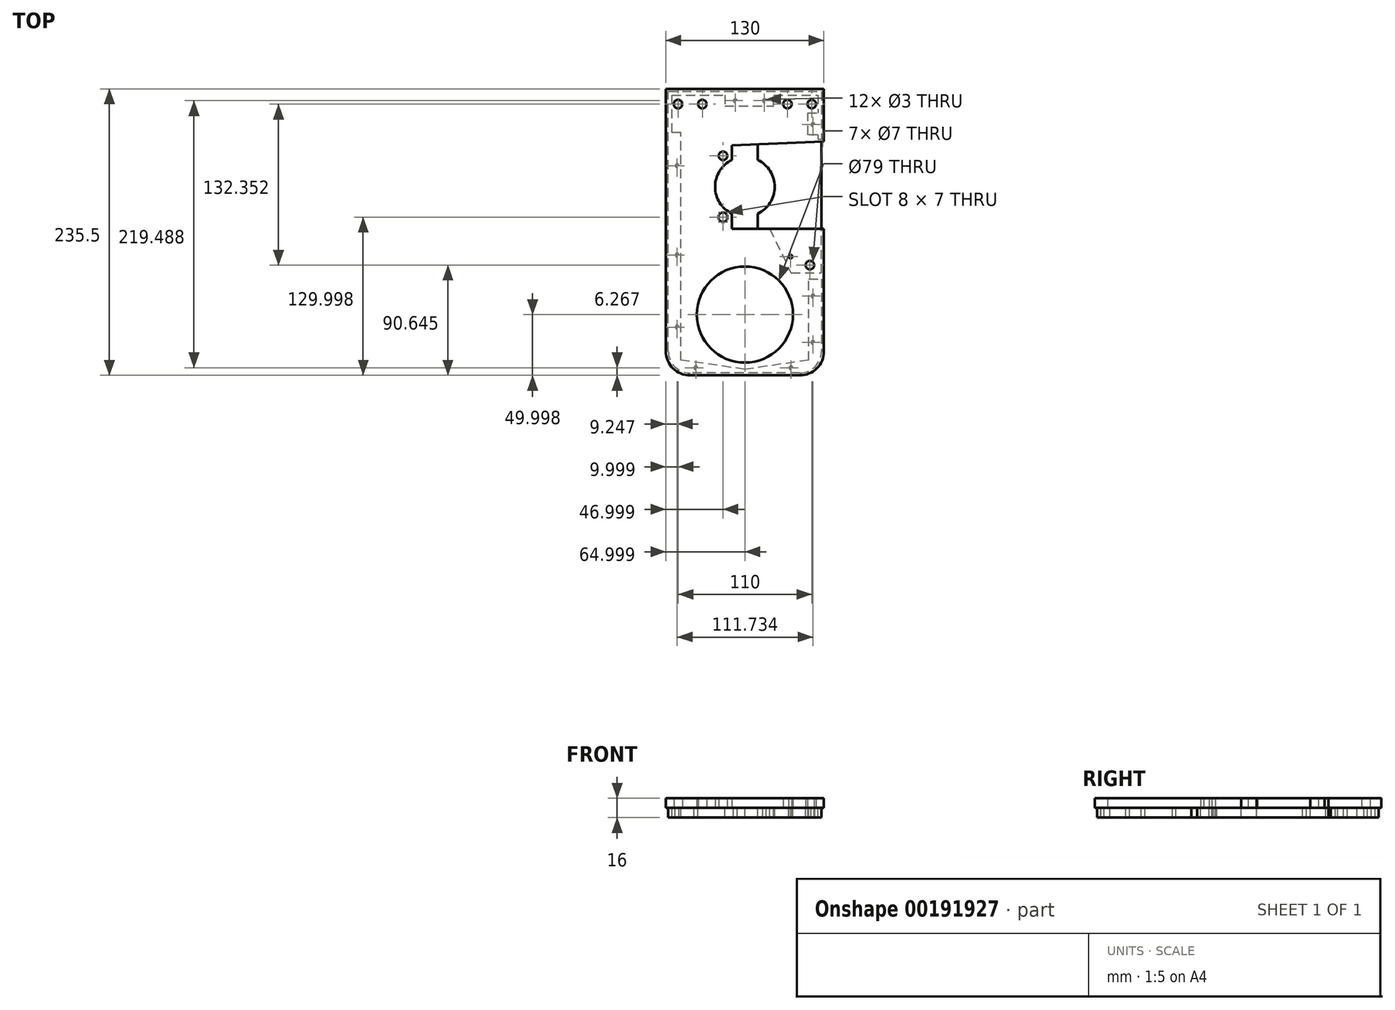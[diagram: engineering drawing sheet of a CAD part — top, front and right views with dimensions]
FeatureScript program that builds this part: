
annotation { "Feature Type Name" : "Feature", "Feature Type Description" : "" }
export const myFeature = defineFeature(function(context is Context, id is Id, definition is map)
    precondition{}
    {
        {
            var Q0;
            Q0=qCreatedBy(makeId("Top.planeOp"),FACE);
            var sketch = newSketch(context, id + "F0", { "sketchPlane" : qUnion([Q0])});
            skCircle(sketch, "E0", {"center": v(-75.48, 27.05) * mm, "radius": 3.5 * mm});
            skCircle(sketch, "E1", {"center": v(-55.48, 27.05) * mm, "radius": 3.5 * mm});
            skCircle(sketch, "E2", {"center": v(14.52, 27.05) * mm, "radius": 3.5 * mm});
            skCircle(sketch, "E3", {"center": v(34.52, 27.05) * mm, "radius": 3.5 * mm});
            skLineSegment(sketch, "E4", {"start": v(-85.48, 39.55) * mm, "end": v(44.52, 39.55) * mm});
            skLineSegment(sketch, "E5", {"start": v(44.52, 39.55) * mm, "end": v(44.52, 14.55) * mm});
            skLineSegment(sketch, "E6", {"start": v(44.52, 14.55) * mm, "end": v(-31.06, 14.55) * mm});
            skLineSegment(sketch, "E7", {"start": v(-31.06, 14.55) * mm, "end": v(-31.06, -96.45) * mm});
            skLineSegment(sketch, "E8", {"start": v(-85.48, -95.95) * mm, "end": v(-85.48, 39.55) * mm});
            skLineSegment(sketch, "E9", {"start": v(-85.48, -95.95) * mm, "end": v(-85.48, -195.95) * mm});
            skLineSegment(sketch, "E10", {"start": v(-85.48, -195.95) * mm, "end": v(44.52, -195.95) * mm});
            skLineSegment(sketch, "E11", {"start": v(44.52, -195.95) * mm, "end": v(44.52, -96.45) * mm});
            skLineSegment(sketch, "E12", {"start": v(44.52, -96.45) * mm, "end": v(-31.06, -96.45) * mm});
            skCircle(sketch, "E13", {"center": v(-20.48, -145.95) * mm, "radius": 39.5 * mm});
            skLineSegment(sketch, "E14", {"start": v(-85.48, -95.95) * mm, "end": v(44.52, -195.95) * mm, "construction": true});
            skLineSegment(sketch, "E15", {"start": v(-85.48, -195.95) * mm, "end": v(44.52, -96.45) * mm, "construction": true});
            skLineSegment(sketch, "E16", {"start": v(-20.48, 39.55) * mm, "end": v(-20.48, -195.95) * mm, "construction": true});
            skLineSegment(sketch, "E17", {"start": v(-85.48, -40.95) * mm, "end": v(48.26, -40.95) * mm, "construction": true});
            skCircle(sketch, "E18", {"center": v(-20.48, -40.95) * mm, "radius": 21.5 * mm, "construction": true});
            skLineSegment(sketch, "E19", {"start": v(-38.48, -15.45) * mm, "end": v(-2.48, -15.45) * mm, "construction": true});
            skLineSegment(sketch, "E20", {"start": v(-2.48, -15.45) * mm, "end": v(-2.48, -66.45) * mm, "construction": true});
            skLineSegment(sketch, "E21", {"start": v(-2.48, -66.45) * mm, "end": v(-38.48, -66.45) * mm, "construction": true});
            skLineSegment(sketch, "E22", {"start": v(-38.48, -66.45) * mm, "end": v(-38.48, -15.45) * mm, "construction": true});
            skCircle(sketch, "E23", {"center": v(-38.48, -15.45) * mm, "radius": 3.5 * mm});
            skCircle(sketch, "E24", {"center": v(-38.48, -66.45) * mm, "radius": 3.5 * mm});
            skCircle(sketch, "E25.0", {"center": v(-20.48, -40.95) * mm, "radius": 24.5 * mm});
            skCircle(sketch, "E26", {"center": v(-38.48, -65.45) * mm, "radius": 3.5 * mm});
            skLineSegment(sketch, "E27", {"start": v(-41.98, -66.45) * mm, "end": v(-41.98, -65.45) * mm});
            skLineSegment(sketch, "E28", {"start": v(-34.98, -66.45) * mm, "end": v(-34.98, -65.45) * mm});
            skLineSegment(sketch, "E29", {"start": v(44.52, 14.55) * mm, "end": v(44.52, -19.45) * mm});
            skLineSegment(sketch, "E30", {"start": v(44.52, -19.45) * mm, "end": v(8.15, -19.45) * mm});
            skLineSegment(sketch, "E31", {"start": v(8.15, -19.45) * mm, "end": v(6.73, 14.55) * mm});
            skLineSegment(sketch, "E32", {"start": v(-31.06, -75.45) * mm, "end": v(44.52, -75.45) * mm});
            skLineSegment(sketch, "E33", {"start": v(44.52, -75.45) * mm, "end": v(44.52, -96.45) * mm});
            skLineSegment(sketch, "E34", {"start": v(-31.06, -6.86) * mm, "end": v(7.56, -5.25) * mm});
            skLineSegment(sketch, "E35", {"start": v(7.56, -5.25) * mm, "end": v(44.52, -3.7) * mm});
            skCircle(sketch, "E36", {"center": v(32.95, -105.3) * mm, "radius": 3.5 * mm});
            skSolve(sketch);
        }
        {
            var Q0;
            Q0=makeQuery(id+"F0.imprint","IMPRINT",FACE,{"disambiguationData":[TD([[makeQuery(id+"F0.imprint","IMPRINT",EDGE,{"derivedFrom":sQuery(id+"F0.wireOp",EDGE,"E0")}),-1.0]])]});
            var Q1;
            {var subQ0=sQuery(id+"F0.wireOp",EDGE,"ye42K3yO-AjDR-pxzV-AlUx-Db0uiflmWcsa");Q1=makeQuery(id+"F0.imprint","IMPRINT",FACE,{"disambiguationData":[TD([[makeQuery(id+"F0.imprint","IMPRINT",EDGE,{"derivedFrom":subQ0}),1.0]])]});}
            var Q2;
            {var subQ0=sQuery(id+"F0.wireOp",EDGE,"E12");Q2=makeQuery(id+"F0.imprint","IMPRINT",FACE,{"disambiguationData":[TD([[makeQuery(id+"F0.imprint","IMPRINT",EDGE,{"derivedFrom":subQ0}),-1.0]])]});}
            var Q3;
            {var subQ0=sQuery(id+"F0.wireOp",EDGE,"E6");Q3=makeQuery(id+"F0.imprint","IMPRINT",FACE,{"disambiguationData":[TD([[makeQuery(id+"F0.imprint","IMPRINT",EDGE,{"derivedFrom":subQ0}),1.0]])]});}
            extrude(context, id + "F1", {"entities" : qUnion([Q0, Q1, Q2, Q3]), "depth" : 8 * mm});
        }
        {
            var Q0;
            Q0=makeQuery(id+"F1.opExtrude","SWEPT_EDGE",EDGE,{"disambiguationData":[OSD([sQuery(id+"F0.wireOp",EDGE,"E9"),sQuery(id+"F0.wireOp",EDGE,"E10")])]});
            var Q1;
            Q1=makeQuery(id+"F1.opExtrude","SWEPT_EDGE",EDGE,{"disambiguationData":[OSD([sQuery(id+"F0.wireOp",EDGE,"E11"),sQuery(id+"F0.wireOp",EDGE,"E12")])]});
            var Q2;
            Q2=makeQuery(id+"F1.opExtrude","SWEPT_EDGE",EDGE,{"disambiguationData":[OSD([sQuery(id+"F0.wireOp",EDGE,"E10"),sQuery(id+"F0.wireOp",EDGE,"E11")])]});
            fillet(context, id + "F2", {"entities" : qUnion([Q0, Q1, Q2]), "radius" : 20 * mm, "tangentPropagation" : true, "allowEdgeOverflow" : false});
        }
        {
            var Q0;
            Q0=makeQuery(id+"F1.opExtrude","CAP_FACE",FACE,{"disambiguationData":[OSD([sQuery(id+"F0.wireOp",EDGE,"E0"),sQuery(id+"F0.wireOp",EDGE,"E1"),sQuery(id+"F0.wireOp",EDGE,"E2"),sQuery(id+"F0.wireOp",EDGE,"E3"),sQuery(id+"F0.wireOp",EDGE,"E4"),sQuery(id+"F0.wireOp",EDGE,"E5"),sQuery(id+"F0.wireOp",EDGE,"E7"),sQuery(id+"F0.wireOp",EDGE,"E8"),sQuery(id+"F0.wireOp",EDGE,"E9"),sQuery(id+"F0.wireOp",EDGE,"E10"),sQuery(id+"F0.wireOp",EDGE,"E11"),sQuery(id+"F0.wireOp",EDGE,"E13"),sQuery(id+"F0.wireOp",EDGE,"E23"),sQuery(id+"F0.wireOp",EDGE,"E24"),sQuery(id+"F0.wireOp",EDGE,"E25.0"),sQuery(id+"F0.wireOp",EDGE,"E26"),sQuery(id+"F0.wireOp",EDGE,"E27"),sQuery(id+"F0.wireOp",EDGE,"E28"),sQuery(id+"F0.wireOp",EDGE,"E29"),sQuery(id+"F0.wireOp",EDGE,"E32"),sQuery(id+"F0.wireOp",EDGE,"E33"),sQuery(id+"F0.wireOp",EDGE,"E34"),sQuery(id+"F0.wireOp",EDGE,"E35"),sQuery(id+"F0.wireOp",EDGE,"E36")])],"isStart":true});
            var sketch = newSketch(context, id + "F3", { "sketchPlane" : qUnion([Q0])});
            skLineSegment(sketch, "E37.0", {"start": v(39.52, -34.55) * mm, "end": v(39.52, 1.79) * mm});
            skLineSegment(sketch, "E37.1", {"start": v(-80.48, -34.55) * mm, "end": v(39.52, -34.55) * mm});
            skLineSegment(sketch, "E37.2", {"start": v(-80.48, 175.95) * mm, "end": v(-80.48, -34.55) * mm});
            skLineSegment(sketch, "E37.3", {"start": v(39.52, 175.95) * mm, "end": v(39.52, 77.45) * mm});
            skArc(sketch, "E37.4", {"start": v(39.52, 175.95) * mm, "mid": v(35.13, 186.56) * mm, "end": v(24.52, 190.95) * mm});
            skLineSegment(sketch, "E37.5", {"start": v(-65.48, 190.95) * mm, "end": v(24.52, 190.95) * mm});
            skArc(sketch, "E37.6", {"start": v(-65.48, 190.95) * mm, "mid": v(-76.09, 186.56) * mm, "end": v(-80.48, 175.95) * mm});
            skArc(sketch, "E38.0", {"start": v(42.52, 175.95) * mm, "mid": v(37.25, 188.68) * mm, "end": v(24.52, 193.95) * mm});
            skLineSegment(sketch, "E38.1", {"start": v(42.52, -37.55) * mm, "end": v(42.52, 1.79) * mm});
            skLineSegment(sketch, "E38.2", {"start": v(-83.48, -37.55) * mm, "end": v(42.52, -37.55) * mm});
            skLineSegment(sketch, "E38.3", {"start": v(-83.48, 175.95) * mm, "end": v(-83.48, -37.55) * mm});
            skArc(sketch, "E38.4", {"start": v(-65.48, 193.95) * mm, "mid": v(-78.2, 188.68) * mm, "end": v(-83.48, 175.95) * mm});
            skLineSegment(sketch, "E38.5", {"start": v(42.52, 1.79) * mm, "end": v(-33.06, 4.95) * mm});
            skLineSegment(sketch, "E38.6", {"start": v(24.52, 193.95) * mm, "end": v(-65.48, 193.95) * mm});
            skLineSegment(sketch, "E38.7", {"start": v(-33.06, 4.95) * mm, "end": v(-33.06, 22.3) * mm});
            skArc(sketch, "E38.8", {"start": v(-33.06, 22.3) * mm, "mid": v(-42.98, 40.95) * mm, "end": v(-33.06, 59.6) * mm});
            skLineSegment(sketch, "E38.9", {"start": v(-33.06, 59.6) * mm, "end": v(-33.06, 77.45) * mm});
            skLineSegment(sketch, "E38.10", {"start": v(-33.06, 77.45) * mm, "end": v(42.52, 77.45) * mm});
            skLineSegment(sketch, "E38.11", {"start": v(42.52, 77.45) * mm, "end": v(42.52, 175.95) * mm});
            skLineSegment(sketch, "E39", {"start": v(39.52, 77.45) * mm, "end": v(42.52, 77.45) * mm});
            skLineSegment(sketch, "E40", {"start": v(39.52, 1.79) * mm, "end": v(42.52, 1.79) * mm});
            skLineSegment(sketch, "E41", {"start": v(39.52, 116.59) * mm, "end": v(42.52, 116.59) * mm});
            skLineSegment(sketch, "E42", {"start": v(24.52, 190.95) * mm, "end": v(39.52, 175.95) * mm});
            skLineSegment(sketch, "E43", {"start": v(-65.48, 190.95) * mm, "end": v(-80.48, 175.95) * mm});
            skLineSegment(sketch, "E44", {"start": v(32.02, 183.45) * mm, "end": v(32.02, 116.59) * mm});
            skLineSegment(sketch, "E45", {"start": v(32.02, 116.59) * mm, "end": v(39.52, 116.59) * mm});
            skLineSegment(sketch, "E46", {"start": v(32.02, 183.45) * mm, "end": v(-20.48, 190.95) * mm});
            skLineSegment(sketch, "E47", {"start": v(-72.98, 183.45) * mm, "end": v(-72.98, -3.75) * mm});
            skLineSegment(sketch, "E48", {"start": v(-72.98, -3.75) * mm, "end": v(-83.48, -3.75) * mm});
            skLineSegment(sketch, "E49", {"start": v(-36.99, -34.55) * mm, "end": v(-36.99, -25.55) * mm});
            skLineSegment(sketch, "E50", {"start": v(-36.99, -25.55) * mm, "end": v(3.21, -25.55) * mm});
            skLineSegment(sketch, "E51", {"start": v(3.21, -25.55) * mm, "end": v(3.21, -34.55) * mm});
            skLineSegment(sketch, "E52", {"start": v(-20.48, 190.95) * mm, "end": v(-72.98, 183.45) * mm});
            skLineSegment(sketch, "E53", {"start": v(39.52, -29.73) * mm, "end": v(34.1, -34.55) * mm});
            skLineSegment(sketch, "E54", {"start": v(-80.48, -29.93) * mm, "end": v(-73.16, -34.55) * mm});
            skLineSegment(sketch, "E55", {"start": v(39.52, -1.75) * mm, "end": v(31.23, -1.75) * mm});
            skLineSegment(sketch, "E56", {"start": v(31.23, -1.75) * mm, "end": v(31.23, -19.82) * mm});
            skLineSegment(sketch, "E57", {"start": v(31.23, -19.82) * mm, "end": v(39.52, -19.82) * mm});
            skCircle(sketch, "E58", {"center": v(35.5, 168.95) * mm, "radius": 1.5 * mm});
            skCircle(sketch, "E59", {"center": v(35.5, 130.7) * mm, "radius": 1.5 * mm});
            skCircle(sketch, "E60", {"center": v(-60.8, 189.68) * mm, "radius": 1.5 * mm});
            skCircle(sketch, "E61", {"center": v(-76.23, 156.28) * mm, "radius": 1.5 * mm});
            skCircle(sketch, "E62", {"center": v(-76.23, 97.05) * mm, "radius": 1.5 * mm});
            skCircle(sketch, "E63", {"center": v(-76.23, 23.57) * mm, "radius": 1.5 * mm});
            skCircle(sketch, "E64", {"center": v(-28.39, -3.6) * mm, "radius": 1.5 * mm});
            skCircle(sketch, "E65", {"center": v(-28.39, -29.8) * mm, "radius": 1.5 * mm});
            skCircle(sketch, "E66", {"center": v(35.5, -10.2) * mm, "radius": 1.5 * mm});
            skCircle(sketch, "E67", {"center": v(17.42, 189.68) * mm, "radius": 1.5 * mm});
            skCircle(sketch, "E68", {"center": v(-4.42, -29.8) * mm, "radius": 1.5 * mm});
            skSolve(sketch);
        }
        {
            var Q0;
            Q0=makeQuery(id+"F3.imprint","IMPRINT",FACE,{"disambiguationData":[TD([[makeQuery(id+"F3.imprint","IMPRINT",EDGE,{"derivedFrom":sQuery(id+"F3.wireOp",EDGE,"E37.0")}),-1.0]])]});
            var Q1;
            {var subQ0=sQuery(id+"F3.wireOp",EDGE,"E37.4");Q1=makeQuery(id+"F3.imprint","IMPRINT",FACE,{"disambiguationData":[TD([[makeQuery(id+"F3.imprint","IMPRINT",EDGE,{"derivedFrom":subQ0}),-1.0]])]});}
            var Q2;
            {var subQ0=sQuery(id+"F3.wireOp",EDGE,"E37.4");Q2=makeQuery(id+"F3.imprint","IMPRINT",FACE,{"disambiguationData":[TD([[makeQuery(id+"F3.imprint","IMPRINT",EDGE,{"derivedFrom":subQ0}),1.0]])]});}
            var Q3;
            {var subQ3=sQuery(id+"F3.wireOp",EDGE,"E46");Q3=makeQuery(id+"F3.imprint","IMPRINT",FACE,{"disambiguationData":[TD([[makeQuery(id+"F3.imprint","IMPRINT",EDGE,{"derivedFrom":subQ3}),-1.0]])]});}
            var Q4;
            {var subQ4=sQuery(id+"F3.wireOp",EDGE,"E44");Q4=makeQuery(id+"F3.imprint","IMPRINT",FACE,{"disambiguationData":[TD([[makeQuery(id+"F3.imprint","IMPRINT",EDGE,{"derivedFrom":subQ4}),1.0]])]});}
            var Q5;
            {var subQ0=sQuery(id+"F3.wireOp",EDGE,"E37.6");Q5=makeQuery(id+"F3.imprint","IMPRINT",FACE,{"disambiguationData":[TD([[makeQuery(id+"F3.imprint","IMPRINT",EDGE,{"derivedFrom":subQ0}),1.0]])]});}
            var Q6;
            {var subQ5=sQuery(id+"F3.wireOp",EDGE,"E47");Q6=makeQuery(id+"F3.imprint","IMPRINT",FACE,{"disambiguationData":[TD([[makeQuery(id+"F3.imprint","IMPRINT",EDGE,{"derivedFrom":subQ5}),-1.0]])]});}
            var Q7;
            {var subQ0=sQuery(id+"F3.wireOp",EDGE,"E49");Q7=makeQuery(id+"F3.imprint","IMPRINT",FACE,{"disambiguationData":[TD([[makeQuery(id+"F3.imprint","IMPRINT",EDGE,{"derivedFrom":subQ0}),-1.0]])]});}
            var Q8;
            {var subQ3=sQuery(id+"F3.wireOp",EDGE,"E52");Q8=makeQuery(id+"F3.imprint","IMPRINT",FACE,{"disambiguationData":[TD([[makeQuery(id+"F3.imprint","IMPRINT",EDGE,{"derivedFrom":subQ3}),-1.0]])]});}
            var Q9;
            {var subQ0=sQuery(id+"F3.wireOp",EDGE,"E55");Q9=makeQuery(id+"F3.imprint","IMPRINT",FACE,{"disambiguationData":[TD([[makeQuery(id+"F3.imprint","IMPRINT",EDGE,{"derivedFrom":subQ0}),1.0]])]});}
            extrude(context, id + "F4", {"entities" : qUnion([Q0, Q1, Q2, Q3, Q4, Q5, Q6, Q7, Q8, Q9]), "depth" : 8 * mm});
        }
        {
            var Q0;
            Q0=makeQuery(id+"F1.opExtrude","CAP_FACE",FACE,{"disambiguationData":[OSD([sQuery(id+"F0.wireOp",EDGE,"E0"),sQuery(id+"F0.wireOp",EDGE,"E1"),sQuery(id+"F0.wireOp",EDGE,"E2"),sQuery(id+"F0.wireOp",EDGE,"E3"),sQuery(id+"F0.wireOp",EDGE,"E4"),sQuery(id+"F0.wireOp",EDGE,"E5"),sQuery(id+"F0.wireOp",EDGE,"E7"),sQuery(id+"F0.wireOp",EDGE,"E8"),sQuery(id+"F0.wireOp",EDGE,"E9"),sQuery(id+"F0.wireOp",EDGE,"E10"),sQuery(id+"F0.wireOp",EDGE,"E11"),sQuery(id+"F0.wireOp",EDGE,"E13"),sQuery(id+"F0.wireOp",EDGE,"E23"),sQuery(id+"F0.wireOp",EDGE,"E24"),sQuery(id+"F0.wireOp",EDGE,"E25.0"),sQuery(id+"F0.wireOp",EDGE,"E26"),sQuery(id+"F0.wireOp",EDGE,"E27"),sQuery(id+"F0.wireOp",EDGE,"E28"),sQuery(id+"F0.wireOp",EDGE,"E29"),sQuery(id+"F0.wireOp",EDGE,"E32"),sQuery(id+"F0.wireOp",EDGE,"E33"),sQuery(id+"F0.wireOp",EDGE,"E34"),sQuery(id+"F0.wireOp",EDGE,"E35"),sQuery(id+"F0.wireOp",EDGE,"E36")])],"isStart":true});
            var sketch = newSketch(context, id + "F5", { "sketchPlane" : qUnion([Q0])});
            skCircle(sketch, "E69", {"center": v(32.95, 105.3) * mm, "radius": 3.5 * mm});
            skLineSegment(sketch, "E70", {"start": v(42.52, 111.81) * mm, "end": v(42.52, 3.79) * mm});
            skLineSegment(sketch, "E71", {"start": v(42.52, 3.79) * mm, "end": v(0, 5.57) * mm});
            skLineSegment(sketch, "E72", {"start": v(0, 75.45) * mm, "end": v(17.52, 111.81) * mm});
            skLineSegment(sketch, "E73", {"start": v(17.52, 111.81) * mm, "end": v(42.52, 111.81) * mm});
            skCircle(sketch, "E74", {"center": v(17.08, 98.33) * mm, "radius": 1.5 * mm});
            skLineSegment(sketch, "E75", {"start": v(0, 75.45) * mm, "end": v(-9.9, 75.45) * mm});
            skLineSegment(sketch, "E76", {"start": v(-9.9, 75.45) * mm, "end": v(-9.9, 5.98) * mm});
            skLineSegment(sketch, "E77", {"start": v(-9.9, 5.98) * mm, "end": v(42.52, 3.79) * mm});
            skSolve(sketch);
        }
        {
            var Q0;
            Q0=makeQuery(id+"F5.imprint","IMPRINT",FACE,{"disambiguationData":[TD([[makeQuery(id+"F5.imprint","IMPRINT",EDGE,{"derivedFrom":sQuery(id+"F5.wireOp",EDGE,"E74")}),1.0]])]});
            extrude(context, id + "F6", {"entities" : qUnion([Q0]), "operationType" : NewBodyOperationType.REMOVE, "oppositeDirection" : true, "depth" : 25 * mm});
        }
        {
            var Q0;
            Q0 = qSketchRegion(id + "F5", true);
            extrude(context, id + "F7", {"entities" : qUnion([Q0]), "depth" : 8 * mm});
        }
        {
            var Q0;
            {var subQ0=sQuery(id+"F0.wireOp",EDGE,"E25.0");var subQ1=sQuery(id+"F0.wireOp",EDGE,"E7");var subQ2=makeQuery(id+"F0.imprint","INTERSECT",VERTEX,{"disambiguationData":[OD(0.0)],"derivedFrom":[subQ1,subQ0]});Q0=makeQuery(id+"F0.imprint","IMPRINT",FACE,{"disambiguationData":[TD([[makeQuery(id+"F0.imprint","IMPRINT",EDGE,{"disambiguationData":[TD([[subQ2,-1.0]])],"derivedFrom":subQ1}),1.0]])]});}
            extrude(context, id + "F8", {"entities" : qUnion([Q0]), "operationType" : NewBodyOperationType.REMOVE, "oppositeDirection" : true, "depth" : 25 * mm});
        }
    });
